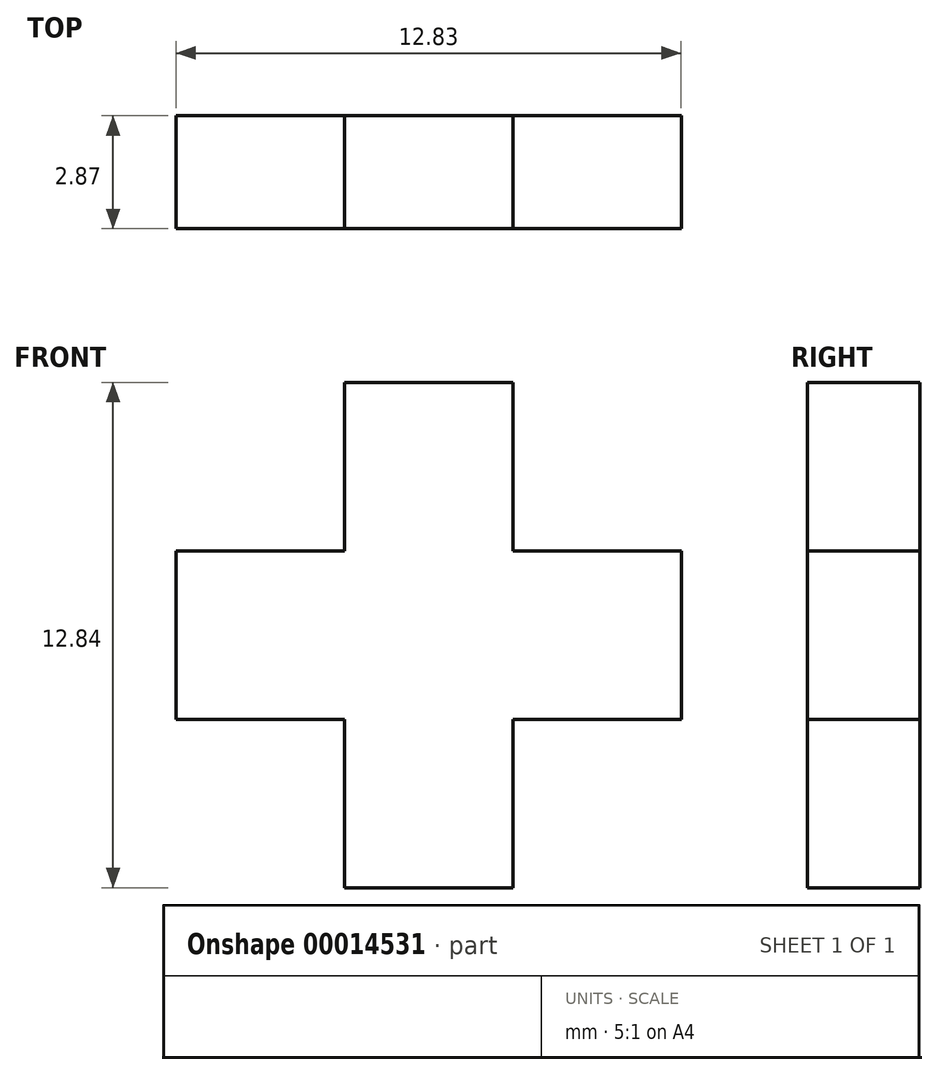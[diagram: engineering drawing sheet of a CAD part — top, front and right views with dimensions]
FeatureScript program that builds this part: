
annotation { "Feature Type Name" : "Feature", "Feature Type Description" : "" }
export const myFeature = defineFeature(function(context is Context, id is Id, definition is map)
    precondition{}
    {
        {
            var Q0;
            Q0=qCreatedBy(makeId("Front.planeOp"),FACE);
            var sketch = newSketch(context, id + "F0", { "sketchPlane" : qUnion([Q0])});
            skLineSegment(sketch, "E0", {"start": v(-37.22, 28.1) * mm, "end": v(-37.22, 23.82) * mm});
            skLineSegment(sketch, "E1", {"start": v(-37.22, 23.82) * mm, "end": v(-41.5, 23.82) * mm});
            skLineSegment(sketch, "E2", {"start": v(-41.5, 23.82) * mm, "end": v(-41.5, 19.54) * mm});
            skLineSegment(sketch, "E3", {"start": v(-41.5, 19.54) * mm, "end": v(-37.22, 19.54) * mm});
            skLineSegment(sketch, "E4", {"start": v(-37.22, 19.54) * mm, "end": v(-37.22, 15.26) * mm});
            skLineSegment(sketch, "E5", {"start": v(-37.22, 15.26) * mm, "end": v(-32.95, 15.26) * mm});
            skLineSegment(sketch, "E6", {"start": v(-32.95, 15.26) * mm, "end": v(-32.95, 19.54) * mm});
            skLineSegment(sketch, "E7", {"start": v(-32.95, 19.54) * mm, "end": v(-28.67, 19.54) * mm});
            skLineSegment(sketch, "E8", {"start": v(-28.67, 19.54) * mm, "end": v(-28.67, 23.82) * mm});
            skLineSegment(sketch, "E9", {"start": v(-28.67, 23.82) * mm, "end": v(-32.95, 23.82) * mm});
            skLineSegment(sketch, "E10", {"start": v(-32.95, 23.82) * mm, "end": v(-32.95, 28.1) * mm});
            skLineSegment(sketch, "E11", {"start": v(-32.95, 28.1) * mm, "end": v(-37.22, 28.1) * mm});
            skSolve(sketch);
        }
        {
            var Q0;
            Q0 = qSketchRegion(id + "F0", true);
            extrude(context, id + "F1", {"entities" : qUnion([Q0]), "depth" : 2.87 * mm});
        }
    });
